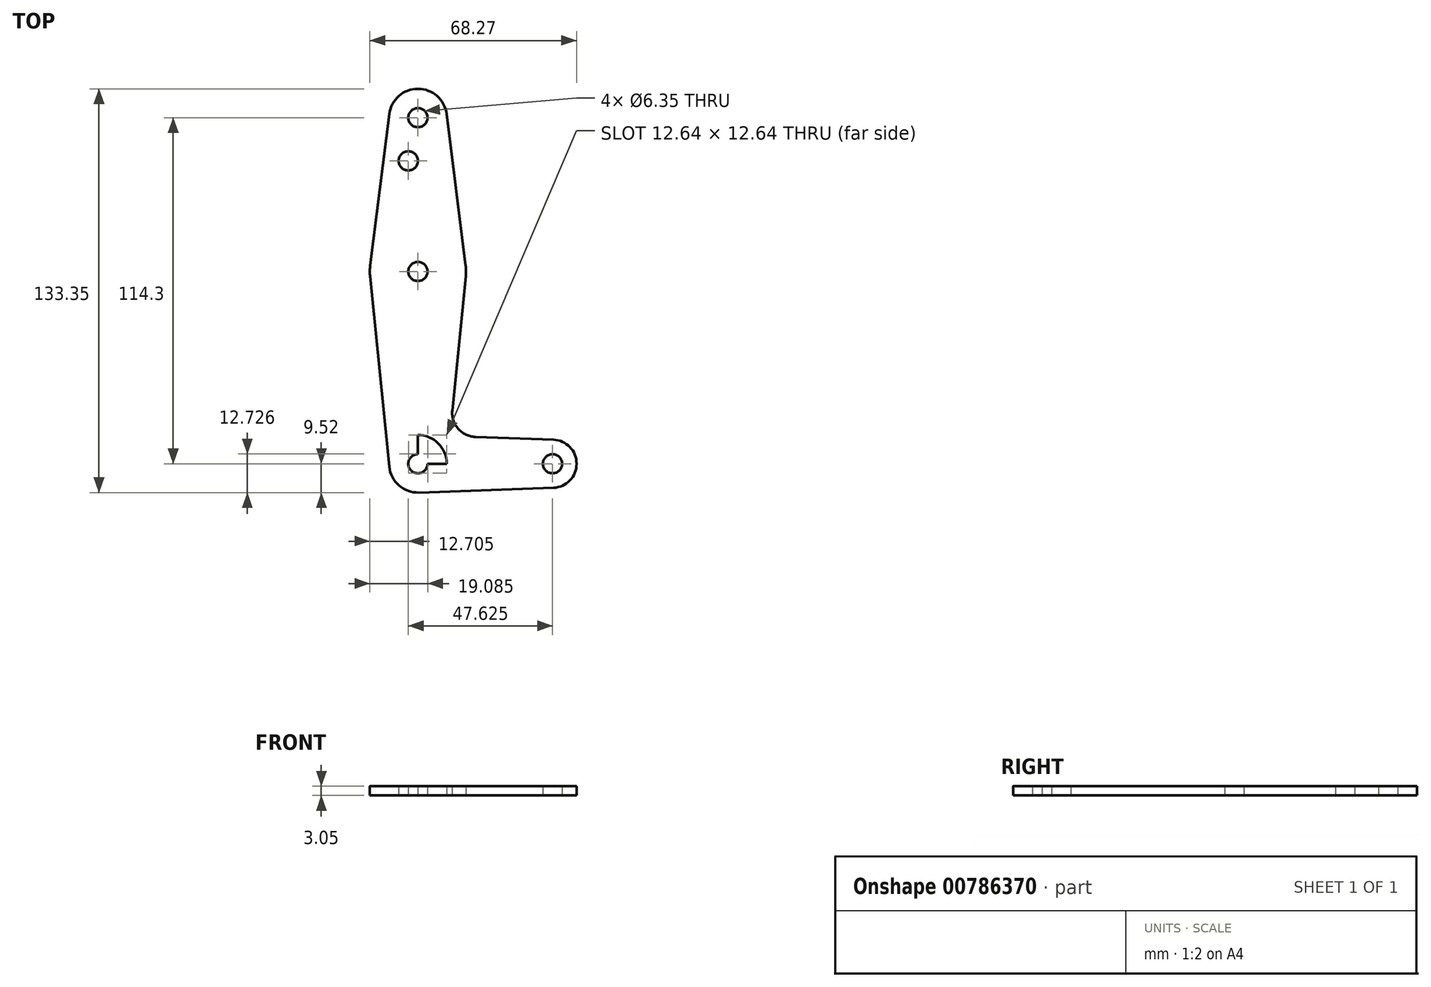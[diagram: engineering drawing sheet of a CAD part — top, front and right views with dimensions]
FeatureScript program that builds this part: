
annotation { "Feature Type Name" : "Feature", "Feature Type Description" : "" }
export const myFeature = defineFeature(function(context is Context, id is Id, definition is map)
    precondition{}
    {
        {
            var Q0;
            Q0=qCreatedBy(makeId("Top.planeOp"),FACE);
            var sketch = newSketch(context, id + "F0", { "sketchPlane" : qUnion([Q0])});
            skLineSegment(sketch, "E0", {"start": v(0, 0) * mm, "end": v(0, 114.3) * mm});
            skLineSegment(sketch, "E1", {"start": v(0, 0) * mm, "end": v(44.45, 0) * mm});
            skCircle(sketch, "E2", {"center": v(0, 114.3) * mm, "radius": 9.53 * mm});
            skCircle(sketch, "E3", {"center": v(0, 63.5) * mm, "radius": 15.88 * mm});
            skCircle(sketch, "E4", {"center": v(0, 0) * mm, "radius": 9.53 * mm});
            skCircle(sketch, "E5", {"center": v(44.45, 0) * mm, "radius": 7.94 * mm});
            skLineSegment(sketch, "E6", {"start": v(-9.45, 115.5) * mm, "end": v(-15.75, 65.48) * mm});
            skLineSegment(sketch, "E7", {"start": v(9.45, 115.5) * mm, "end": v(15.75, 65.48) * mm});
            skLineSegment(sketch, "E8", {"start": v(-15.8, 61.91) * mm, "end": v(-9.48, -0.95) * mm});
            skLineSegment(sketch, "E9", {"start": v(15.8, 61.91) * mm, "end": v(11.34, 17.6) * mm});
            skLineSegment(sketch, "E10", {"start": v(18.97, 8.85) * mm, "end": v(44.73, 7.93) * mm});
            skLineSegment(sketch, "E11", {"start": v(0.34, -9.52) * mm, "end": v(44.73, -7.93) * mm});
            skCircle(sketch, "E12", {"center": v(0, 114.3) * mm, "radius": 3.18 * mm});
            skCircle(sketch, "E13", {"center": v(0, 63.5) * mm, "radius": 3.18 * mm});
            skCircle(sketch, "E14", {"center": v(0, 0) * mm, "radius": 3.18 * mm});
            skCircle(sketch, "E15", {"center": v(44.45, 0) * mm, "radius": 3.18 * mm});
            skCircle(sketch, "E16", {"center": v(-3.18, 100.03) * mm, "radius": 3.18 * mm});
            skArc(sketch, "E17.filletArc", {"start": v(11.34, 17.6) * mm, "mid": v(13.26, 11.57) * mm, "end": v(18.97, 8.85) * mm});
            skSolve(sketch);
        }
        {
            var Q0;
            Q0 = qSketchRegion(id + "F0", true);
            extrude(context, id + "F1", {"entities" : qUnion([Q0]), "depth" : 3.05 * mm, "offsetDistance" : 25.4 * mm});
        }
    });
